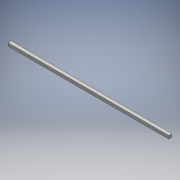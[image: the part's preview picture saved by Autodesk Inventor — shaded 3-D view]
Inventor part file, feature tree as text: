
AUTODESK INVENTOR PART (.ipt)
format: ipt  version: 2016 (Build 200138000, 138)  size: 99,840 bytes
history: native  units: mm
features: extrude x2, sketch x2
ambient origin geometry x8: Origin, YZ Plane, XZ Plane, XY Plane, X Axis, Y Axis, Z Axis, Center Point
bodies: 实体1 (feature_tree)
feature tree (4):
  extrude  "拉伸1"  Depth=15.0mm
  extrude  "拉伸2"  Depth=15.0mm
  sketch  "草图1"  dims[d0=755.0mm d1=15.0mm]
  sketch  "草图2"  dims[d2=15.0mm d3=0.0mm d4=7.5mm d5=7.5mm d6=5.0mm d7=800.0mm d8=0.0mm]
